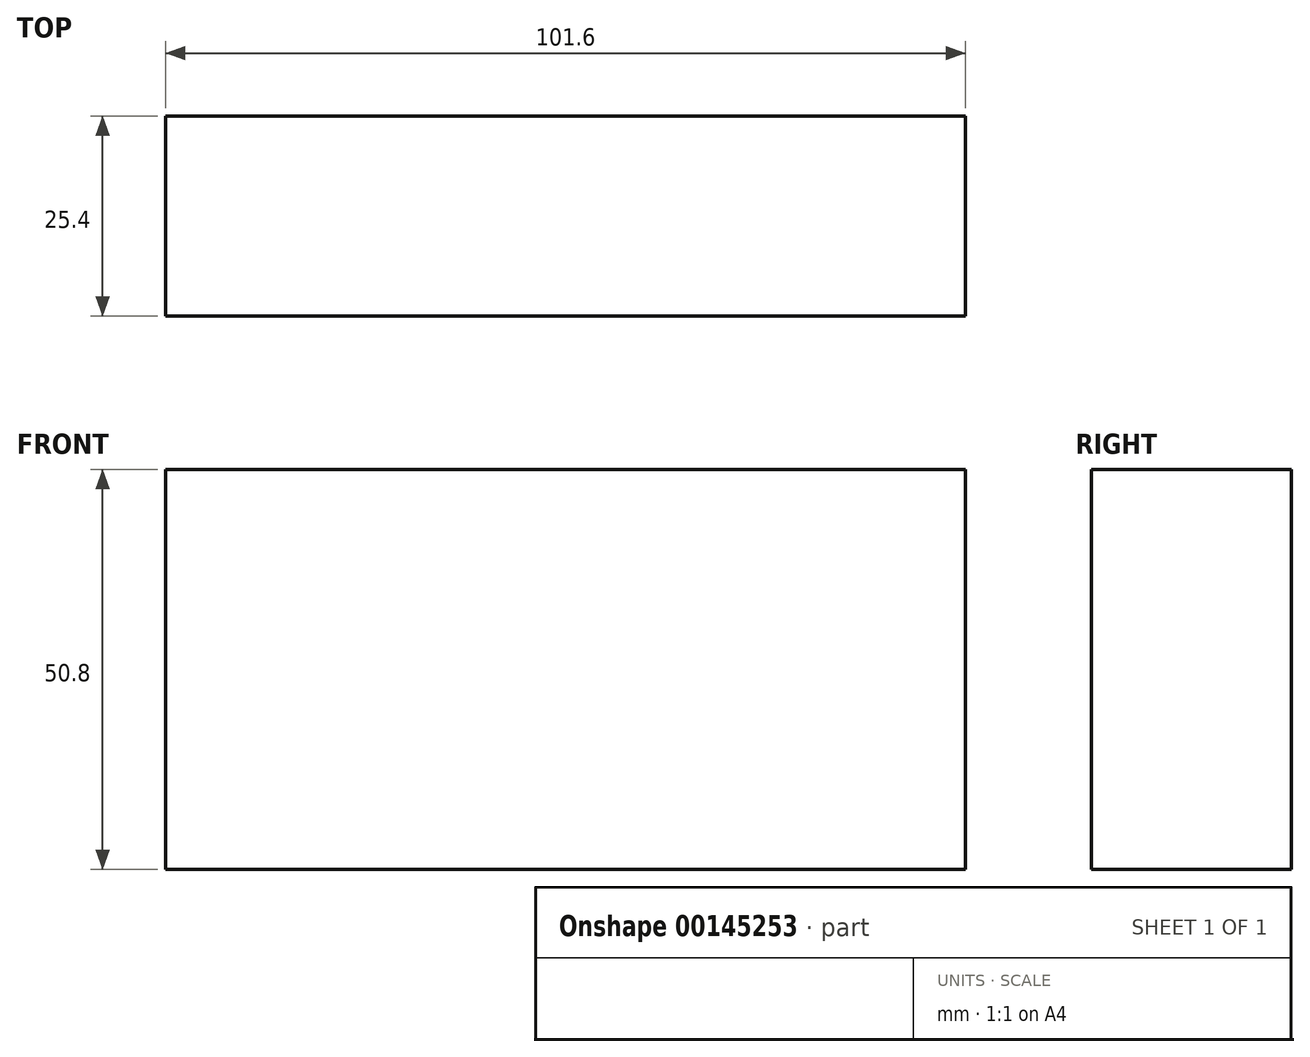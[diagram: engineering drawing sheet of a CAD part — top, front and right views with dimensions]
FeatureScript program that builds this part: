
annotation { "Feature Type Name" : "Feature", "Feature Type Description" : "" }
export const myFeature = defineFeature(function(context is Context, id is Id, definition is map)
    precondition{}
    {
        {
            var Q0;
            Q0=qCreatedBy(makeId("Front.planeOp"),FACE);
            var sketch = newSketch(context, id + "F0", { "sketchPlane" : qUnion([Q0])});
            skLineSegment(sketch, "E0.bottom", {"start": v(50.8, 25.4) * mm, "end": v(-50.8, 25.4) * mm});
            skLineSegment(sketch, "E0.top", {"start": v(50.8, -25.4) * mm, "end": v(-50.8, -25.4) * mm});
            skLineSegment(sketch, "E0.left", {"start": v(50.8, 25.4) * mm, "end": v(50.8, -25.4) * mm});
            skLineSegment(sketch, "E0.right", {"start": v(-50.8, 25.4) * mm, "end": v(-50.8, -25.4) * mm});
            skPoint(sketch, "E0.middle", {"position": v(0, 0) * mm});
            skSolve(sketch);
        }
        {
            var Q0;
            Q0 = qSketchRegion(id + "F0", true);
            extrude(context, id + "F1", {"entities" : qUnion([Q0]), "endBound" : BoundingType.SYMMETRIC, "depth" : 25.4 * mm});
        }
    });
